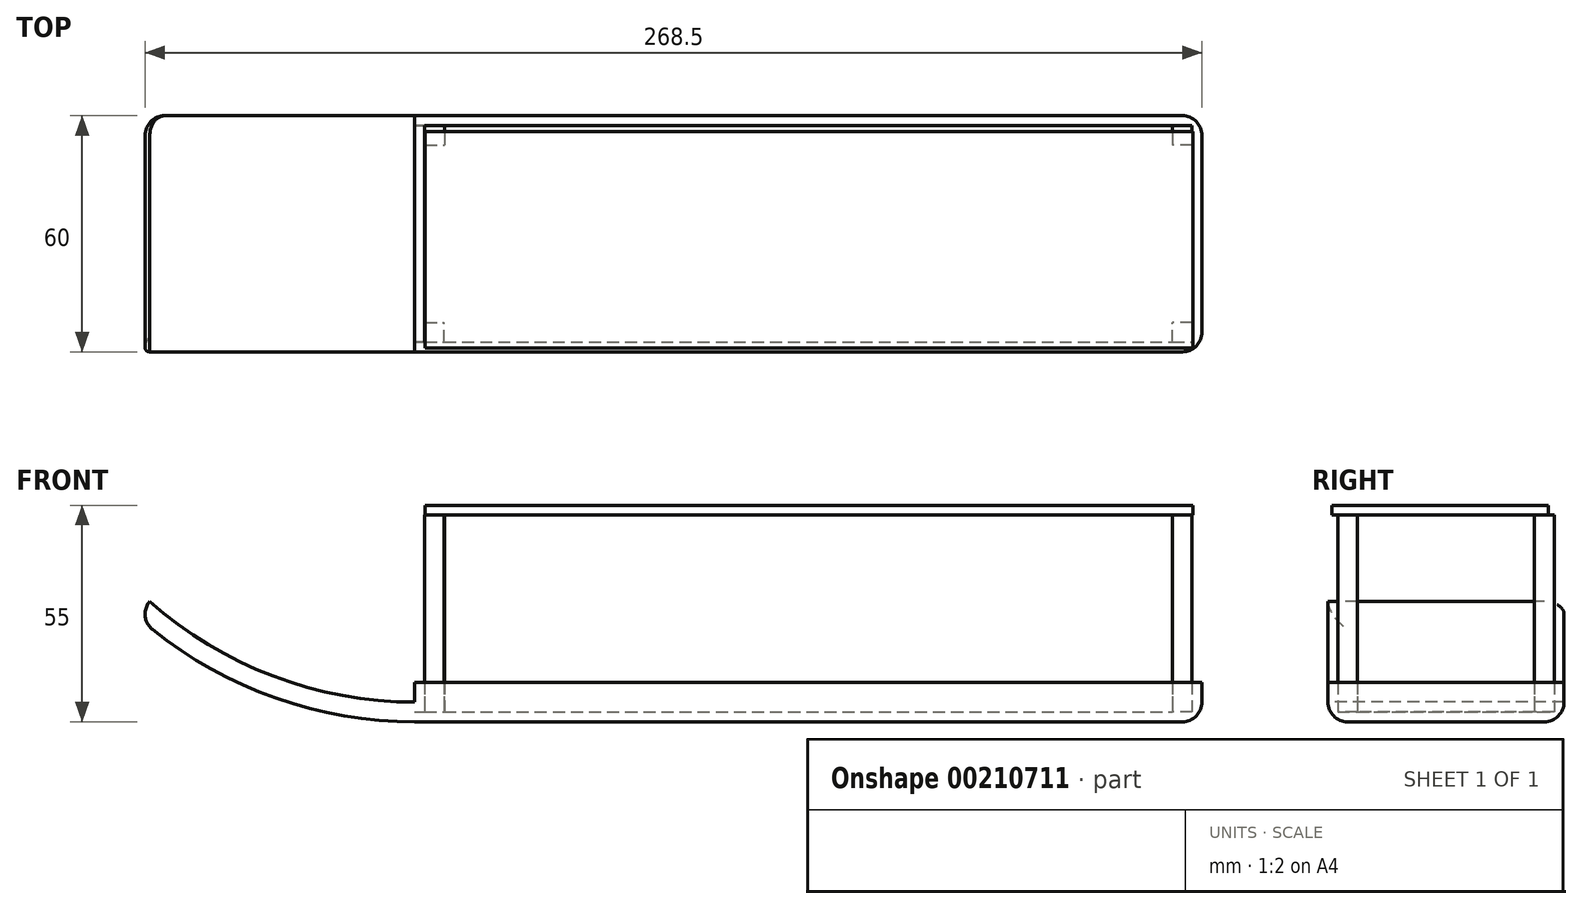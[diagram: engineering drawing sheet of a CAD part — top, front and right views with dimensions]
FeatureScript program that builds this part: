
annotation { "Feature Type Name" : "Feature", "Feature Type Description" : "" }
export const myFeature = defineFeature(function(context is Context, id is Id, definition is map)
    precondition{}
    {
        {
            var Q0;
            Q0=qCreatedBy(makeId("Top.planeOp"),FACE);
            var sketch = newSketch(context, id + "F0", { "sketchPlane" : qUnion([Q0])});
            skLineSegment(sketch, "E0.bottom", {"start": v(-100, 30) * mm, "end": v(100, 30) * mm});
            skLineSegment(sketch, "E0.top", {"start": v(-100, -30) * mm, "end": v(100, -30) * mm});
            skLineSegment(sketch, "E0.left", {"start": v(-100, 30) * mm, "end": v(-100, -30) * mm});
            skLineSegment(sketch, "E0.right", {"start": v(100, 30) * mm, "end": v(100, -30) * mm});
            skPoint(sketch, "E0.middle", {"position": v(0, 0) * mm});
            skSolve(sketch);
        }
        {
            var Q0;
            Q0=makeQuery(id+"F0.imprint","IMPRINT",FACE,{"disambiguationData":[TD([[makeQuery(id+"F0.imprint","IMPRINT",EDGE,{"derivedFrom":sQuery(id+"F0.wireOp",EDGE,"E0.bottom")}),-1.0]])]});
            extrude(context, id + "F1", {"entities" : qUnion([Q0]), "depth" : 5 * mm});
        }
        {
            var Q0;
            Q0=makeQuery(id+"F1.opExtrude","SWEPT_FACE",FACE,{"disambiguationData":[OSD([sQuery(id+"F0.wireOp",EDGE,"E0.left")])]});
            var sketch = newSketch(context, id + "F2", { "sketchPlane" : qUnion([Q0])});
            skLineSegment(sketch, "E1.bottom", {"start": v(-30, 5) * mm, "end": v(30, 5) * mm});
            skLineSegment(sketch, "E1.top", {"start": v(-30, 0) * mm, "end": v(30, 0) * mm});
            skLineSegment(sketch, "E1.left", {"start": v(-30, 5) * mm, "end": v(-30, 0) * mm});
            skLineSegment(sketch, "E1.right", {"start": v(30, 5) * mm, "end": v(30, 0) * mm});
            skSolve(sketch);
        }
        {
            var Q0;
            Q0=makeQuery(id+"F1.opExtrude","SWEPT_FACE",FACE,{"disambiguationData":[OSD([sQuery(id+"F0.wireOp",EDGE,"E0.top")])]});
            var sketch = newSketch(context, id + "F3", { "sketchPlane" : qUnion([Q0])});
            skArc(sketch, "E2", {"start": v(-170.64, 26.85) * mm, "mid": v(-137.78, 6.94) * mm, "end": v(-100, 0) * mm});
            skSolve(sketch);
        }
        {
            var Q0;
            Q0=makeQuery(id+"F2.imprint","IMPRINT",FACE,{"disambiguationData":[TD([[makeQuery(id+"F2.imprint","IMPRINT",EDGE,{"derivedFrom":sQuery(id+"F2.wireOp",EDGE,"E1.bottom")}),-1.0]])]});
            var Q1;
            Q1=sQuery(id+"F3.wireOp",EDGE,"VhbGXAAn-pJU9-2EqL-hbCo-qS7XswDItT7m");
            var Q2;
            Q2=sQuery(id+"F3.wireOp",EDGE,"E2");
            sweep(context, id + "F4", {"operationType" : NewBodyOperationType.ADD, "profiles" : qUnion([Q0]), "path" : qUnion([Q1, Q2])});
        }
        {
            var Q0;
            Q0=makeQuery(id+"F1.opExtrude","CAP_FACE",FACE,{"disambiguationData":[OSD([sQuery(id+"F0.wireOp",EDGE,"E0.bottom"),sQuery(id+"F0.wireOp",EDGE,"E0.top"),sQuery(id+"F0.wireOp",EDGE,"E0.left"),sQuery(id+"F0.wireOp",EDGE,"E0.right")])],"isStart":false});
            var sketch = newSketch(context, id + "F5", { "sketchPlane" : qUnion([Q0])});
            skLineSegment(sketch, "E3.bottom", {"start": v(-100, 30) * mm, "end": v(100, 30) * mm});
            skLineSegment(sketch, "E3.top", {"start": v(-100, -30) * mm, "end": v(100, -30) * mm});
            skLineSegment(sketch, "E3.left", {"start": v(-100, 30) * mm, "end": v(-100, -30) * mm});
            skLineSegment(sketch, "E3.right", {"start": v(100, 30) * mm, "end": v(100, -30) * mm});
            skSolve(sketch);
        }
        {
            var Q0;
            Q0=makeQuery(id+"F5.imprint","IMPRINT",FACE,{"disambiguationData":[TD([[makeQuery(id+"F5.imprint","IMPRINT",EDGE,{"derivedFrom":sQuery(id+"F5.wireOp",EDGE,"E3.bottom")}),-1.0]])]});
            extrude(context, id + "F6", {"entities" : qUnion([Q0]), "operationType" : NewBodyOperationType.ADD, "depth" : 5 * mm});
        }
        {
            var Q0;
            Q0=makeQuery(id+"F6.opExtrude","CAP_FACE",FACE,{"disambiguationData":[OSD([sQuery(id+"F5.wireOp",EDGE,"E3.bottom"),sQuery(id+"F5.wireOp",EDGE,"E3.top"),sQuery(id+"F5.wireOp",EDGE,"E3.left"),sQuery(id+"F5.wireOp",EDGE,"E3.right")])],"isStart":false});
            shell(context, id + "F7", {"entities" : qUnion([Q0]), "thickness" : 2.5 * mm});
        }
        {
            var Q0;
            Q0=makeQuery(id+"F4.opSweep","SWEPT_EDGE",EDGE,{"disambiguationData":[OSD([sQuery(id+"F2.wireOp",EDGE,"E1.top"),sQuery(id+"F2.wireOp",EDGE,"E1.right"),sQuery(id+"F3.wireOp",EDGE,"E2")])]});
            fillet(context, id + "F8", {"entities" : qUnion([Q0]), "radius" : 5 * mm, "tangentPropagation" : true, "allowEdgeOverflow" : false});
        }
        {
            var Q0;
            Q0=makeQuery(id+"F4.opSweep","CAP_EDGE",EDGE,{"disambiguationData":[OSD([sQuery(id+"F2.wireOp",EDGE,"E1.top"),sQuery(id+"F3.wireOp",VERTEX,"E2.start")])],"isStart":false});
            fillet(context, id + "F9", {"entities" : qUnion([Q0]), "radius" : 5 * mm, "tangentPropagation" : true, "allowEdgeOverflow" : false});
        }
        {
            var Q0;
            Q0=makeQuery(id+"F4.opSweep","SWEPT_EDGE",EDGE,{"disambiguationData":[OSD([sQuery(id+"F2.wireOp",EDGE,"E1.top"),sQuery(id+"F2.wireOp",EDGE,"E1.left"),sQuery(id+"F3.wireOp",EDGE,"E2")])]});
            fillet(context, id + "F10", {"entities" : qUnion([Q0]), "radius" : 5 * mm, "tangentPropagation" : true, "allowEdgeOverflow" : false});
        }
        {
            var Q0;
            Q0=makeQuery(id+"F1.opExtrude","CAP_EDGE",EDGE,{"disambiguationData":[OSD([sQuery(id+"F0.wireOp",EDGE,"E0.right")])],"isStart":true});
            fillet(context, id + "F11", {"entities" : qUnion([Q0]), "radius" : 5 * mm, "tangentPropagation" : true, "allowEdgeOverflow" : false});
        }
        {
            var Q0;
            Q0=makeQuery(id+"F7.opShell","OFFSET_FACE",FACE,{"disambiguationData":[OSD([sQuery(id+"F0.wireOp",EDGE,"E0.bottom"),sQuery(id+"F0.wireOp",EDGE,"E0.top"),sQuery(id+"F0.wireOp",EDGE,"E0.left"),sQuery(id+"F0.wireOp",EDGE,"E0.right")])]});
            var sketch = newSketch(context, id + "F12", { "sketchPlane" : qUnion([Q0])});
            skLineSegment(sketch, "E4.bottom", {"start": v(-97.44, 27.5) * mm, "end": v(-92.44, 27.5) * mm});
            skLineSegment(sketch, "E4.top", {"start": v(-97.44, 22.5) * mm, "end": v(-92.44, 22.5) * mm});
            skLineSegment(sketch, "E4.left", {"start": v(-97.44, 27.5) * mm, "end": v(-97.44, 22.5) * mm});
            skLineSegment(sketch, "E4.right", {"start": v(-92.44, 27.5) * mm, "end": v(-92.44, 22.5) * mm});
            skLineSegment(sketch, "E5.bottom", {"start": v(-97.5, -27.5) * mm, "end": v(-92.5, -27.5) * mm});
            skLineSegment(sketch, "E5.top", {"start": v(-97.5, -22.5) * mm, "end": v(-92.5, -22.5) * mm});
            skLineSegment(sketch, "E5.left", {"start": v(-97.5, -27.5) * mm, "end": v(-97.5, -22.5) * mm});
            skLineSegment(sketch, "E5.right", {"start": v(-92.5, -27.5) * mm, "end": v(-92.5, -22.5) * mm});
            skLineSegment(sketch, "E6.bottom", {"start": v(97.5, -27.5) * mm, "end": v(92.5, -27.5) * mm});
            skLineSegment(sketch, "E6.top", {"start": v(97.5, -22.5) * mm, "end": v(92.5, -22.5) * mm});
            skLineSegment(sketch, "E6.left", {"start": v(97.5, -27.5) * mm, "end": v(97.5, -22.5) * mm});
            skLineSegment(sketch, "E6.right", {"start": v(92.5, -27.5) * mm, "end": v(92.5, -22.5) * mm});
            skLineSegment(sketch, "E7.bottom", {"start": v(97.5, 27.5) * mm, "end": v(92.5, 27.5) * mm});
            skLineSegment(sketch, "E7.top", {"start": v(97.5, 22.5) * mm, "end": v(92.5, 22.5) * mm});
            skLineSegment(sketch, "E7.left", {"start": v(97.5, 27.5) * mm, "end": v(97.5, 22.5) * mm});
            skLineSegment(sketch, "E7.right", {"start": v(92.5, 27.5) * mm, "end": v(92.5, 22.5) * mm});
            skSolve(sketch);
        }
        {
            var Q0;
            Q0 = qSketchRegion(id + "F12", true);
            extrude(context, id + "F13", {"entities" : qUnion([Q0]), "operationType" : NewBodyOperationType.ADD, "depth" : 50 * mm});
        }
        {
            var Q0;
            Q0=qCreatedBy(makeId("Top.planeOp"),FACE);
            cPlane(context, id + "F14", {"entities" : qUnion([Q0]), "cplaneType" : CPlaneType.OFFSET, "offset" : 55 * mm, "width" : 150 * mm, "height" : 150 * mm});
        }
        {
            var Q0;
            Q0=qCreatedBy(id+"F14.planeOp",FACE);
            var sketch = newSketch(context, id + "F15", { "sketchPlane" : qUnion([Q0])});
            skLineSegment(sketch, "E8.bottom", {"start": v(-97.33, -29) * mm, "end": v(97.67, -29) * mm});
            skLineSegment(sketch, "E8.top", {"start": v(-97.33, 26) * mm, "end": v(97.67, 26) * mm});
            skLineSegment(sketch, "E8.left", {"start": v(-97.33, -29) * mm, "end": v(-97.33, 26) * mm});
            skLineSegment(sketch, "E8.right", {"start": v(97.67, -29) * mm, "end": v(97.67, 26) * mm});
            skSolve(sketch);
        }
        {
            var Q0;
            Q0=makeQuery(id+"F15.imprint","IMPRINT",FACE,{"disambiguationData":[TD([[makeQuery(id+"F15.imprint","IMPRINT",EDGE,{"derivedFrom":sQuery(id+"F15.wireOp",EDGE,"E8.bottom")}),1.0]])]});
            extrude(context, id + "F16", {"entities" : qUnion([Q0]), "oppositeDirection" : true, "depth" : 2.5 * mm});
        }
    });
